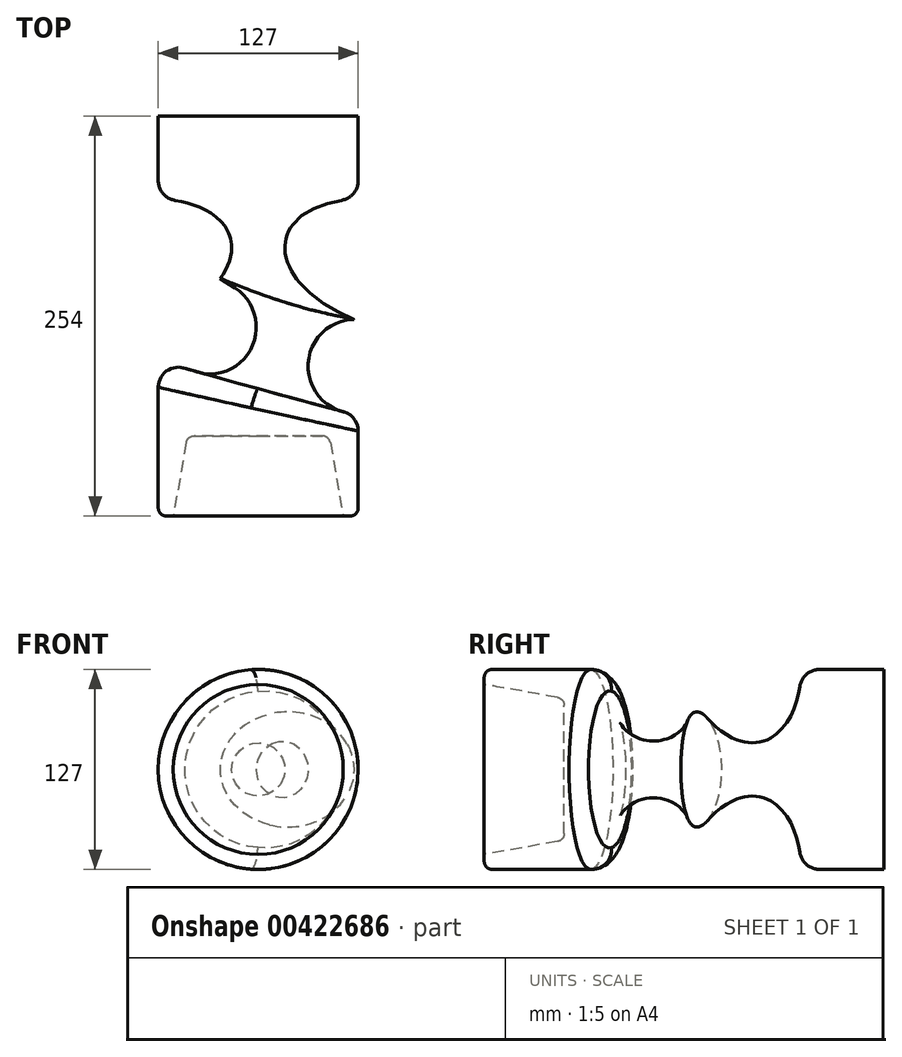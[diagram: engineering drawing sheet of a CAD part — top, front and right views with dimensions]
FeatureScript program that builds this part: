
annotation { "Feature Type Name" : "Feature", "Feature Type Description" : "" }
export const myFeature = defineFeature(function(context is Context, id is Id, definition is map)
    precondition{}
    {
        {
            var Q0;
            Q0=qCreatedBy(makeId("Top.planeOp"),FACE);
            var sketch = newSketch(context, id + "F0", { "sketchPlane" : qUnion([Q0])});
            skLineSegment(sketch, "E0", {"start": v(0, 0) * mm, "end": v(0, 50.8) * mm});
            skLineSegment(sketch, "E1", {"start": v(0, 50.8) * mm, "end": v(0, 111.75) * mm});
            skLineSegment(sketch, "E2", {"start": v(0, 50.8) * mm, "end": v(15.67, 109.27) * mm});
            skSolve(sketch);
        }
        {
            var Q0;
            Q0=qCreatedBy(makeId("Top.planeOp"),FACE);
            var Q1;
            Q1=sQuery(id+"F0.wireOp",EDGE,"E0");
            cPlane(context, id + "F1", {"entities" : qUnion([Q0, Q1]), "cplaneType" : CPlaneType.LINE_ANGLE, "offset" : 25.4 * mm, "angle" : 120 * degree, "oppositeDirection" : true, "width" : 152.4 * mm, "height" : 152.4 * mm});
        }
        {
            var Q0;
            Q0=qCreatedBy(makeId("Right.planeOp"),FACE);
            var Q1;
            Q1=sQuery(id+"F0.wireOp",EDGE,"E0");
            cPlane(context, id + "F2", {"entities" : qUnion([Q0, Q1]), "cplaneType" : CPlaneType.LINE_ANGLE, "offset" : 25.4 * mm, "angle" : 30 * degree, "width" : 152.4 * mm, "height" : 152.4 * mm});
        }
        {
            var Q0;
            Q0=qCreatedBy(id+"F2.planeOp",FACE);
            var sketch = newSketch(context, id + "F3", { "sketchPlane" : qUnion([Q0])});
            skLineSegment(sketch, "E3", {"start": v(-152.4, 0) * mm, "end": v(-203.2, 0) * mm});
            skLineSegment(sketch, "E4", {"start": v(-152.4, 0) * mm, "end": v(-199.38, -12.59) * mm});
            skSolve(sketch);
        }
        {
            var Q0;
            Q0=qCreatedBy(makeId("Front.planeOp"),FACE);
            var sketch = newSketch(context, id + "F4", { "sketchPlane" : qUnion([Q0])});
            skCircle(sketch, "E5", {"center": v(0, 0) * mm, "radius": 63.5 * mm});
            skSolve(sketch);
        }
        {
            var Q0;
            Q0 = qSketchRegion(id + "F4", true);
            extrude(context, id + "F5", {"entities" : qUnion([Q0]), "oppositeDirection" : true, "depth" : 254 * mm});
        }
        {
            var Q0;
            Q0=qCreatedBy(makeId("Top.planeOp"),FACE);
            var sketch = newSketch(context, id + "F6", { "sketchPlane" : qUnion([Q0])});
            skArc(sketch, "E6", {"start": v(59.8, 124.87) * mm, "mid": v(31.69, 96.97) * mm, "end": v(56.08, 65.76) * mm});
            skLineSegment(sketch, "E7", {"start": v(59.8, 124.87) * mm, "end": v(166.62, 130.79) * mm});
            skLineSegment(sketch, "E8", {"start": v(166.62, 130.79) * mm, "end": v(166.62, 45.5) * mm});
            skLineSegment(sketch, "E9", {"start": v(166.62, 45.5) * mm, "end": v(56.08, 65.76) * mm});
            skSolve(sketch);
        }
        {
            var Q0;
            Q0=makeQuery(id+"F6.imprint","IMPRINT",FACE,{"disambiguationData":[TD([[makeQuery(id+"F6.imprint","IMPRINT",EDGE,{"derivedFrom":sQuery(id+"F6.wireOp",EDGE,"E6")}),1.0]])]});
            var Q1;
            Q1=sQuery(id+"F0.wireOp",EDGE,"E2");
            revolve(context, id + "F7", {"operationType" : NewBodyOperationType.REMOVE, "entities" : qUnion([Q0]), "axis" : qUnion([Q1]), "revolveType" : RevolveType.FULL, "oppositeDirection" : true});
        }
        {
            var Q0;
            Q0=qCreatedBy(makeId("Top.planeOp"),FACE);
            var sketch = newSketch(context, id + "F8", { "sketchPlane" : qUnion([Q0])});
            skEllipse(sketch, "E10", {"center": v(85.52, 159.02) * mm, "majorRadius": 70.05 * mm, "minorRadius": 40.16 * mm, "majorAxis": v(-0.97, 0.25)});
            skSolve(sketch);
        }
        {
            var Q0;
            Q0=makeQuery(id+"F8.imprint","IMPRINT",FACE,{"disambiguationData":[TD([[makeQuery(id+"F8.imprint","IMPRINT",EDGE,{"derivedFrom":sQuery(id+"F8.wireOp",EDGE,"E10")}),1.0]])]});
            var Q1;
            Q1=sQuery(id+"F3.wireOp",EDGE,"E3");
            revolve(context, id + "F9", {"operationType" : NewBodyOperationType.REMOVE, "entities" : qUnion([Q0]), "axis" : qUnion([Q1]), "revolveType" : RevolveType.FULL, "oppositeDirection" : true});
        }
        {
            var Q0;
            {var subQ0=sQuery(id+"F4.wireOp",EDGE,"E5");Q0=makeQuery(id+"F9.boolean.opBoolean","INTERSECT",EDGE,{"derivedFrom":[makeQuery(id+"F7.boolean.opBoolean","SPLIT",FACE,{"disambiguationData":[TD([makeQuery(id+"F5.opExtrude","CAP_FACE",FACE,{"disambiguationData":[OSD([subQ0])],"isStart":false})])],"derivedFrom":makeQuery(id+"F5.opExtrude","SWEPT_FACE",FACE,{"disambiguationData":[OSD([subQ0])]})}),makeQuery(id+"F9.opRevolve","SWEPT_FACE",FACE,{"disambiguationData":[OSD([sQuery(id+"F8.wireOp",EDGE,"E10")])]})]});}
            var Q1;
            Q1=makeQuery(id+"F7.boolean.opBoolean","INTERSECT",EDGE,{"derivedFrom":[makeQuery(id+"F5.opExtrude","SWEPT_FACE",FACE,{"disambiguationData":[OSD([sQuery(id+"F4.wireOp",EDGE,"E5")])]}),makeQuery(id+"F7.opRevolve","SWEPT_FACE",FACE,{"disambiguationData":[OSD([sQuery(id+"F6.wireOp",EDGE,"E9")])]})]});
            fillet(context, id + "F10", {"entities" : qUnion([Q0, Q1]), "radius" : 12.7 * mm, "tangentPropagation" : true, "allowEdgeOverflow" : false});
        }
        {
            var Q0;
            Q0=makeQuery(id+"F5.opExtrude","CAP_FACE",FACE,{"disambiguationData":[OSD([sQuery(id+"F4.wireOp",EDGE,"E5")])],"isStart":true});
            var sketch = newSketch(context, id + "F11", { "sketchPlane" : qUnion([Q0])});
            skCircle(sketch, "E11.0", {"center": v(0, 0) * mm, "radius": 53.98 * mm});
            skSolve(sketch);
        }
        {
            var Q0;
            Q0 = qSketchRegion(id + "F11", true);
            extrude(context, id + "F12", {"entities" : qUnion([Q0]), "operationType" : NewBodyOperationType.REMOVE, "oppositeDirection" : true, "depth" : 50.8 * mm, "hasDraft" : true, "draftAngle" : 10 * degree, "draftPullDirection" : true});
        }
        {
            var Q0;
            Q0=makeQuery(id+"F12.boolean.opBoolean","COPY",EDGE,{"derivedFrom":makeQuery(id+"F12.opExtrude","CAP_EDGE",EDGE,{"disambiguationData":[OSD([sQuery(id+"F11.wireOp",EDGE,"E11.0")])],"isStart":true})});
            var Q1;
            Q1=makeQuery(id+"F12.boolean.opBoolean","COPY",EDGE,{"derivedFrom":makeQuery(id+"F12.opExtrude","CAP_EDGE",EDGE,{"disambiguationData":[OSD([sQuery(id+"F11.wireOp",EDGE,"E11.0")])],"isStart":false})});
            fillet(context, id + "F13", {"entities" : qUnion([Q0, Q1]), "radius" : 5.08 * mm, "tangentPropagation" : true, "allowEdgeOverflow" : false});
        }
        {
            var Q0;
            Q0=makeQuery(id+"F5.opExtrude","CAP_EDGE",EDGE,{"disambiguationData":[OSD([sQuery(id+"F4.wireOp",EDGE,"E5")])],"isStart":true});
            fillet(context, id + "F14", {"entities" : qUnion([Q0]), "radius" : 5.08 * mm, "tangentPropagation" : true, "allowEdgeOverflow" : false});
        }
    });
